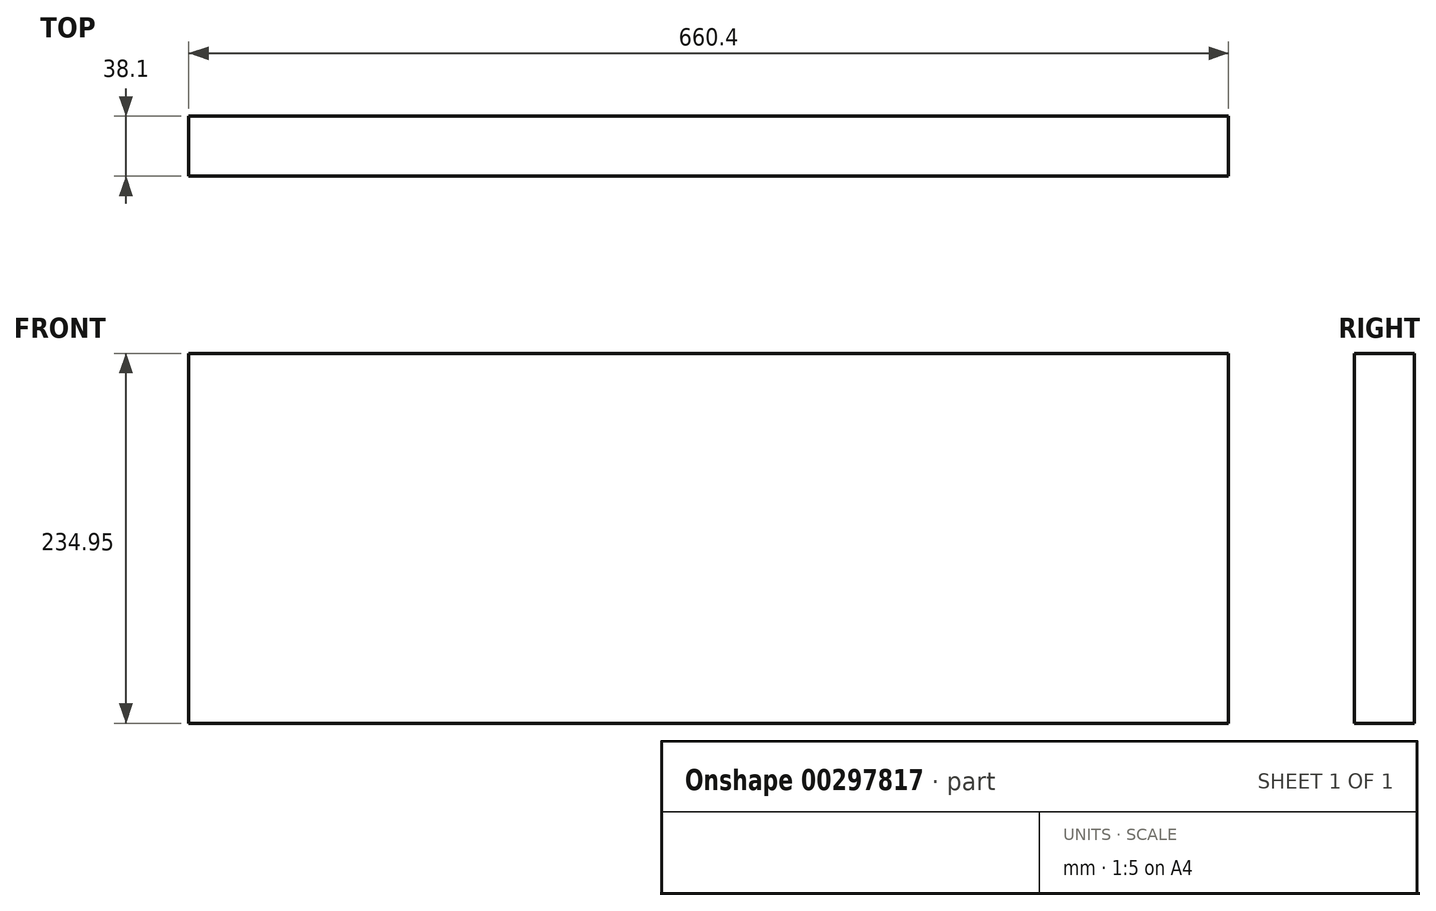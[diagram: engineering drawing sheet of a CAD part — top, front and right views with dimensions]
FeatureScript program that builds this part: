
annotation { "Feature Type Name" : "Feature", "Feature Type Description" : "" }
export const myFeature = defineFeature(function(context is Context, id is Id, definition is map)
    precondition{}
    {
        {
            var Q0;
            Q0=qCreatedBy(makeId("Front.planeOp"),FACE);
            var sketch = newSketch(context, id + "F0", { "sketchPlane" : qUnion([Q0])});
            skLineSegment(sketch, "E0.bottom", {"start": v(0, 0) * mm, "end": v(660.4, 0) * mm});
            skLineSegment(sketch, "E0.top", {"start": v(0, 234.95) * mm, "end": v(660.4, 234.95) * mm});
            skLineSegment(sketch, "E0.left", {"start": v(0, 0) * mm, "end": v(0, 234.95) * mm});
            skLineSegment(sketch, "E0.right", {"start": v(660.4, 0) * mm, "end": v(660.4, 234.95) * mm});
            skSolve(sketch);
        }
        {
            var Q0;
            Q0=makeQuery(id+"F0.imprint","IMPRINT",FACE,{"disambiguationData":[TD([[makeQuery(id+"F0.imprint","IMPRINT",EDGE,{"derivedFrom":sQuery(id+"F0.wireOp",EDGE,"E0.bottom")}),1.0]])]});
            extrude(context, id + "F1", {"entities" : qUnion([Q0]), "depth" : 38.1 * mm});
        }
    });
